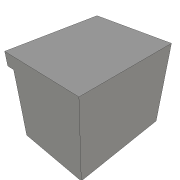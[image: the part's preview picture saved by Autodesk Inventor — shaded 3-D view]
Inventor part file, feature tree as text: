
AUTODESK INVENTOR PART (.ipt)
format: ipt  version: 2016 (Build 200138000, 138)  size: 181,760 bytes
history: native  units: in
note: dims shown in document units (in); Inventor stores cm internally (conversion verified against a paired STEP export)
features: extrude x1, sketch x1, projected_geometry x1, imported_body x1
ambient origin geometry x8: Origin, YZ Plane, XZ Plane, XY Plane, X Axis, Y Axis, Z Axis, Center Point
bodies: Solid1 (feature_tree)
feature tree (4):
  extrude  "Extrusion1"  Depth=0.3937in
  sketch  "Sketch1"  dims[d0=0.0098in d1=0.3937in d2=0.0069in]
  projected_geometry  "Projected Loop1"
  imported_body  "Base1"
